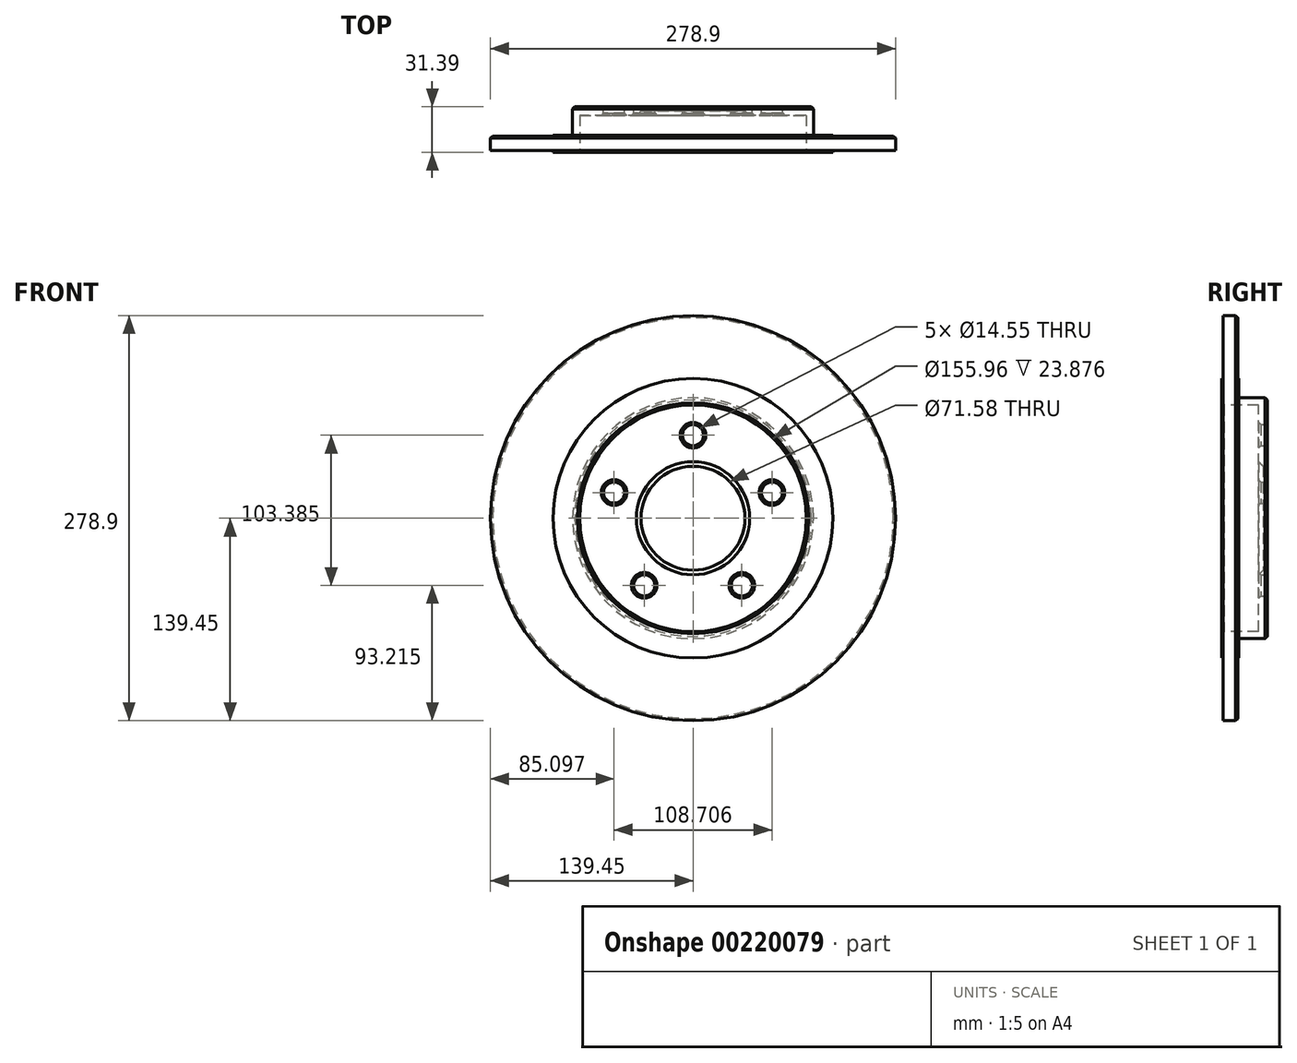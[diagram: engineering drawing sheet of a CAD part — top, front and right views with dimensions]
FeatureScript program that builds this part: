
annotation { "Feature Type Name" : "Feature", "Feature Type Description" : "" }
export const myFeature = defineFeature(function(context is Context, id is Id, definition is map)
    precondition{}
    {
        {
            var Q0;
            Q0=qCreatedBy(makeId("Right.planeOp"),FACE);
            var sketch = newSketch(context, id + "F0", { "sketchPlane" : qUnion([Q0])});
            skLineSegment(sketch, "E0", {"start": v(0, 0) * mm, "end": v(0, 82.93) * mm});
            skLineSegment(sketch, "E1", {"start": v(0, 82.93) * mm, "end": v(-19.63, 82.93) * mm});
            skLineSegment(sketch, "E2", {"start": v(-19.63, 82.93) * mm, "end": v(-19.63, 139.45) * mm});
            skLineSegment(sketch, "E3", {"start": v(-19.63, 139.45) * mm, "end": v(-31.4, 139.45) * mm});
            skLineSegment(sketch, "E4", {"start": v(-31.4, 139.45) * mm, "end": v(-31.4, 77.98) * mm});
            skLineSegment(sketch, "E5", {"start": v(-31.4, 77.98) * mm, "end": v(-6, 77.98) * mm});
            skLineSegment(sketch, "E6", {"start": v(-6, 77.98) * mm, "end": v(-6, 0) * mm});
            skLineSegment(sketch, "E7", {"start": v(-6, 0) * mm, "end": v(0, 0) * mm});
            skLineSegment(sketch, "E8", {"start": v(0, 0) * mm, "end": v(109.01, 0) * mm, "construction": true});
            skSolve(sketch);
        }
        {
            var Q0;
            Q0 = qSketchRegion(id + "F0", true);
            var Q1;
            Q1=sQuery(id+"F0.wireOp",EDGE,"E8");
            revolve(context, id + "F1", {"entities" : qUnion([Q0]), "axis" : qUnion([Q1]), "revolveType" : RevolveType.FULL});
        }
        {
            var Q0;
            Q0=makeQuery(id+"F1.opRevolve","SWEPT_FACE",FACE,{"disambiguationData":[OSD([sQuery(id+"F0.wireOp",EDGE,"E2")])]});
            var sketch = newSketch(context, id + "F2", { "sketchPlane" : qUnion([Q0])});
            skCircle(sketch, "E9.0", {"center": v(0, 0) * mm, "radius": 139.45 * mm, "construction": true});
            skCircle(sketch, "E10", {"center": v(0, 0) * mm, "radius": 96.27 * mm});
            skCircle(sketch, "E11", {"center": v(0, 0) * mm, "radius": 169.8 * mm});
            skSolve(sketch);
        }
        {
            var Q0;
            Q0 = qSketchRegion(id + "F2", true);
            extrude(context, id + "F3", {"entities" : qUnion([Q0]), "operationType" : NewBodyOperationType.REMOVE, "oppositeDirection" : true, "depth" : 0.58 * mm});
        }
        {
            var Q0;
            Q0=makeQuery(id+"F1.opRevolve","SWEPT_FACE",FACE,{"disambiguationData":[OSD([sQuery(id+"F0.wireOp",EDGE,"E4")])]});
            var sketch = newSketch(context, id + "F4", { "sketchPlane" : qUnion([Q0])});
            skCircle(sketch, "E12.0", {"center": v(0, 0) * mm, "radius": 139.45 * mm});
            skCircle(sketch, "E13", {"center": v(0, 0) * mm, "radius": 96.27 * mm});
            skSolve(sketch);
        }
        {
            var Q0;
            Q0 = qSketchRegion(id + "F4", true);
            extrude(context, id + "F5", {"entities" : qUnion([Q0]), "operationType" : NewBodyOperationType.REMOVE, "oppositeDirection" : true, "depth" : 1.07 * mm});
        }
        {
            var Q0;
            Q0=makeQuery(id+"F3.boolean.opBoolean","INTERSECT",EDGE,{"derivedFrom":[makeQuery(id+"F1.opRevolve","SWEPT_FACE",FACE,{"disambiguationData":[OSD([sQuery(id+"F0.wireOp",EDGE,"E3")])]}),makeQuery(id+"F3.opExtrude","CAP_FACE",FACE,{"disambiguationData":[OSD([sQuery(id+"F2.wireOp",EDGE,"E10"),sQuery(id+"F2.wireOp",EDGE,"E11")])],"isStart":false})]});
            var Q1;
            Q1=makeQuery(id+"F5.boolean.opBoolean","COPY",EDGE,{"derivedFrom":makeQuery(id+"F5.opExtrude","CAP_EDGE",EDGE,{"disambiguationData":[OSD([sQuery(id+"F4.wireOp",EDGE,"E12.0")])],"isStart":false})});
            var Q2;
            Q2=makeQuery(id+"F1.opRevolve","SWEPT_EDGE",EDGE,{"disambiguationData":[OSD([sQuery(id+"F0.wireOp",EDGE,"E0"),sQuery(id+"F0.wireOp",EDGE,"E1")])]});
            var Q3;
            Q3=makeQuery(id+"F1.opRevolve","SWEPT_EDGE",EDGE,{"disambiguationData":[OSD([sQuery(id+"F0.wireOp",EDGE,"E4"),sQuery(id+"F0.wireOp",EDGE,"E5")])]});
            chamfer(context, id + "F6", {"entities" : qUnion([Q0, Q1, Q2, Q3]), "width" : 1.52 * mm, "tangentPropagation" : true});
        }
        {
            var Q0;
            Q0=makeQuery(id+"F1.opRevolve","SWEPT_FACE",FACE,{"disambiguationData":[OSD([sQuery(id+"F0.wireOp",EDGE,"E0")])]});
            var sketch = newSketch(context, id + "F7", { "sketchPlane" : qUnion([Q0])});
            skCircle(sketch, "E14.0", {"center": v(0, 0) * mm, "radius": 81.4 * mm, "construction": true});
            skCircle(sketch, "E15", {"center": v(0, 0) * mm, "radius": 35.79 * mm});
            skCircle(sketch, "E16", {"center": v(0, 0) * mm, "radius": 57.15 * mm, "construction": true});
            skCircle(sketch, "E17", {"center": v(0, 57.15) * mm, "radius": 7.28 * mm});
            skCircle(sketch, "E18.1.0", {"center": v(-54.35, 17.66) * mm, "radius": 7.28 * mm});
            skCircle(sketch, "E18.2.0", {"center": v(-33.6, -46.24) * mm, "radius": 7.28 * mm});
            skCircle(sketch, "E18.3.0", {"center": v(33.6, -46.24) * mm, "radius": 7.28 * mm});
            skCircle(sketch, "E18.4.0", {"center": v(54.35, 17.66) * mm, "radius": 7.28 * mm});
            skSolve(sketch);
        }
        {
            var Q0;
            Q0 = qSketchRegion(id + "F7", true);
            extrude(context, id + "F8", {"entities" : qUnion([Q0]), "operationType" : NewBodyOperationType.REMOVE, "oppositeDirection" : true, "depth" : 25.4 * mm});
        }
        {
            var Q0;
            Q0=makeQuery(id+"F8.boolean.opBoolean","COPY",EDGE,{"derivedFrom":makeQuery(id+"F8.opExtrude","CAP_EDGE",EDGE,{"disambiguationData":[OSD([sQuery(id+"F7.wireOp",EDGE,"E17")])],"isStart":true})});
            var Q1;
            Q1=makeQuery(id+"F8.boolean.opBoolean","COPY",EDGE,{"derivedFrom":makeQuery(id+"F8.opExtrude","CAP_EDGE",EDGE,{"disambiguationData":[OSD([sQuery(id+"F7.wireOp",EDGE,"E18.4.0")])],"isStart":true})});
            var Q2;
            Q2=makeQuery(id+"F8.boolean.opBoolean","COPY",EDGE,{"derivedFrom":makeQuery(id+"F8.opExtrude","CAP_EDGE",EDGE,{"disambiguationData":[OSD([sQuery(id+"F7.wireOp",EDGE,"E18.3.0")])],"isStart":true})});
            var Q3;
            Q3=makeQuery(id+"F8.boolean.opBoolean","COPY",EDGE,{"derivedFrom":makeQuery(id+"F8.opExtrude","CAP_EDGE",EDGE,{"disambiguationData":[OSD([sQuery(id+"F7.wireOp",EDGE,"E18.2.0")])],"isStart":true})});
            var Q4;
            Q4=makeQuery(id+"F8.boolean.opBoolean","COPY",EDGE,{"derivedFrom":makeQuery(id+"F8.opExtrude","CAP_EDGE",EDGE,{"disambiguationData":[OSD([sQuery(id+"F7.wireOp",EDGE,"E18.1.0")])],"isStart":true})});
            var Q5;
            Q5=makeQuery(id+"F8.boolean.opBoolean","INTERSECT",EDGE,{"derivedFrom":[makeQuery(id+"F1.opRevolve","SWEPT_FACE",FACE,{"disambiguationData":[OSD([sQuery(id+"F0.wireOp",EDGE,"E6")])]}),makeQuery(id+"F8.opExtrude","SWEPT_FACE",FACE,{"disambiguationData":[OSD([sQuery(id+"F7.wireOp",EDGE,"E18.3.0")])]})]});
            var Q6;
            Q6=makeQuery(id+"F8.boolean.opBoolean","INTERSECT",EDGE,{"derivedFrom":[makeQuery(id+"F1.opRevolve","SWEPT_FACE",FACE,{"disambiguationData":[OSD([sQuery(id+"F0.wireOp",EDGE,"E6")])]}),makeQuery(id+"F8.opExtrude","SWEPT_FACE",FACE,{"disambiguationData":[OSD([sQuery(id+"F7.wireOp",EDGE,"E18.4.0")])]})]});
            var Q7;
            Q7=makeQuery(id+"F8.boolean.opBoolean","INTERSECT",EDGE,{"derivedFrom":[makeQuery(id+"F1.opRevolve","SWEPT_FACE",FACE,{"disambiguationData":[OSD([sQuery(id+"F0.wireOp",EDGE,"E6")])]}),makeQuery(id+"F8.opExtrude","SWEPT_FACE",FACE,{"disambiguationData":[OSD([sQuery(id+"F7.wireOp",EDGE,"E17")])]})]});
            var Q8;
            Q8=makeQuery(id+"F8.boolean.opBoolean","INTERSECT",EDGE,{"derivedFrom":[makeQuery(id+"F1.opRevolve","SWEPT_FACE",FACE,{"disambiguationData":[OSD([sQuery(id+"F0.wireOp",EDGE,"E6")])]}),makeQuery(id+"F8.opExtrude","SWEPT_FACE",FACE,{"disambiguationData":[OSD([sQuery(id+"F7.wireOp",EDGE,"E18.1.0")])]})]});
            var Q9;
            Q9=makeQuery(id+"F8.boolean.opBoolean","INTERSECT",EDGE,{"derivedFrom":[makeQuery(id+"F1.opRevolve","SWEPT_FACE",FACE,{"disambiguationData":[OSD([sQuery(id+"F0.wireOp",EDGE,"E6")])]}),makeQuery(id+"F8.opExtrude","SWEPT_FACE",FACE,{"disambiguationData":[OSD([sQuery(id+"F7.wireOp",EDGE,"E18.2.0")])]})]});
            var Q10;
            Q10=makeQuery(id+"F8.boolean.opBoolean","COPY",EDGE,{"derivedFrom":makeQuery(id+"F8.opExtrude","CAP_EDGE",EDGE,{"disambiguationData":[OSD([sQuery(id+"F7.wireOp",EDGE,"E15")])],"isStart":true})});
            chamfer(context, id + "F9", {"entities" : qUnion([Q0, Q1, Q2, Q3, Q4, Q5, Q6, Q7, Q8, Q9, Q10]), "width" : 1.52 * mm, "tangentPropagation" : true});
        }
        {
            var Q0;
            Q0=makeQuery(id+"F8.boolean.opBoolean","INTERSECT",EDGE,{"derivedFrom":[makeQuery(id+"F1.opRevolve","SWEPT_FACE",FACE,{"disambiguationData":[OSD([sQuery(id+"F0.wireOp",EDGE,"E6")])]}),makeQuery(id+"F8.opExtrude","SWEPT_FACE",FACE,{"disambiguationData":[OSD([sQuery(id+"F7.wireOp",EDGE,"E15")])]})]});
            chamfer(context, id + "F10", {"entities" : qUnion([Q0]), "width" : 3.17 * mm, "tangentPropagation" : true});
        }
    });
